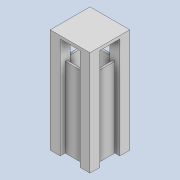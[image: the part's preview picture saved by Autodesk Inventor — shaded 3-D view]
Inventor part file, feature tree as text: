
AUTODESK INVENTOR PART (.ipt)
format: ipt  version: 2021 (Build 250183000, 183)  size: 142,848 bytes
history: native  units: mm
features: extrude x4, sketch x2
ambient origin geometry x8: Origin, YZ Plane, XZ Plane, XY Plane, X Axis, Y Axis, Z Axis, Center Point
bodies: Solid1 (feature_tree)
feature tree (6):
  sketch  "Sketch1"  dims[d0=300.0mm d1=300.0mm]
  extrude  "Extrusion1"  Depth=300.0mm
  extrude  "Extrusion2"  Depth=100.0mm
  extrude  "Extrusion3"  Depth=100.0mm
  extrude  "Extrusion4"  Depth=100.0mm
  sketch  "Sketch2"  dims[d2=100.0mm d3=100.0mm d4=100.0mm d5=100.0mm d6=100.0mm d7=100.0mm d8=1050.0mm d9=0.0mm d10=800.0mm d11=0.0mm d12=30.0mm d13=0.0mm d14=260.0mm d15=10.0mm d16=0.0mm]
